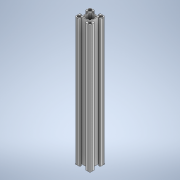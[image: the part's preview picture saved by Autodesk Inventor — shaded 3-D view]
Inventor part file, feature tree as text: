
AUTODESK INVENTOR PART (.ipt)
format: ipt  version: 2020 (Build 240168000, 168)  size: 7,133,696 bytes
history: native  units: in
note: dims shown in document units (in); Inventor stores cm internally (conversion verified against a paired STEP export)
features: extrude x2, sketch x2
ambient origin geometry x8: Origin, YZ Plane, XZ Plane, XY Plane, X Axis, Y Axis, Z Axis, Center Point
bodies: Solid1 (feature_tree)
feature tree (4):
  extrude  "Extrusion1"  Depth=3.875in TaperAngle=0.0deg
  extrude  "Extrusion2"  Depth=15.0625in TaperAngle=0.0deg
  sketch  "Sketch1"  dims[d0=0.5in d1=3.875in d2=0.0in]
  sketch  "Sketch2"  dims[d3=2.217in d4=15.0625in d5=0.0in]
